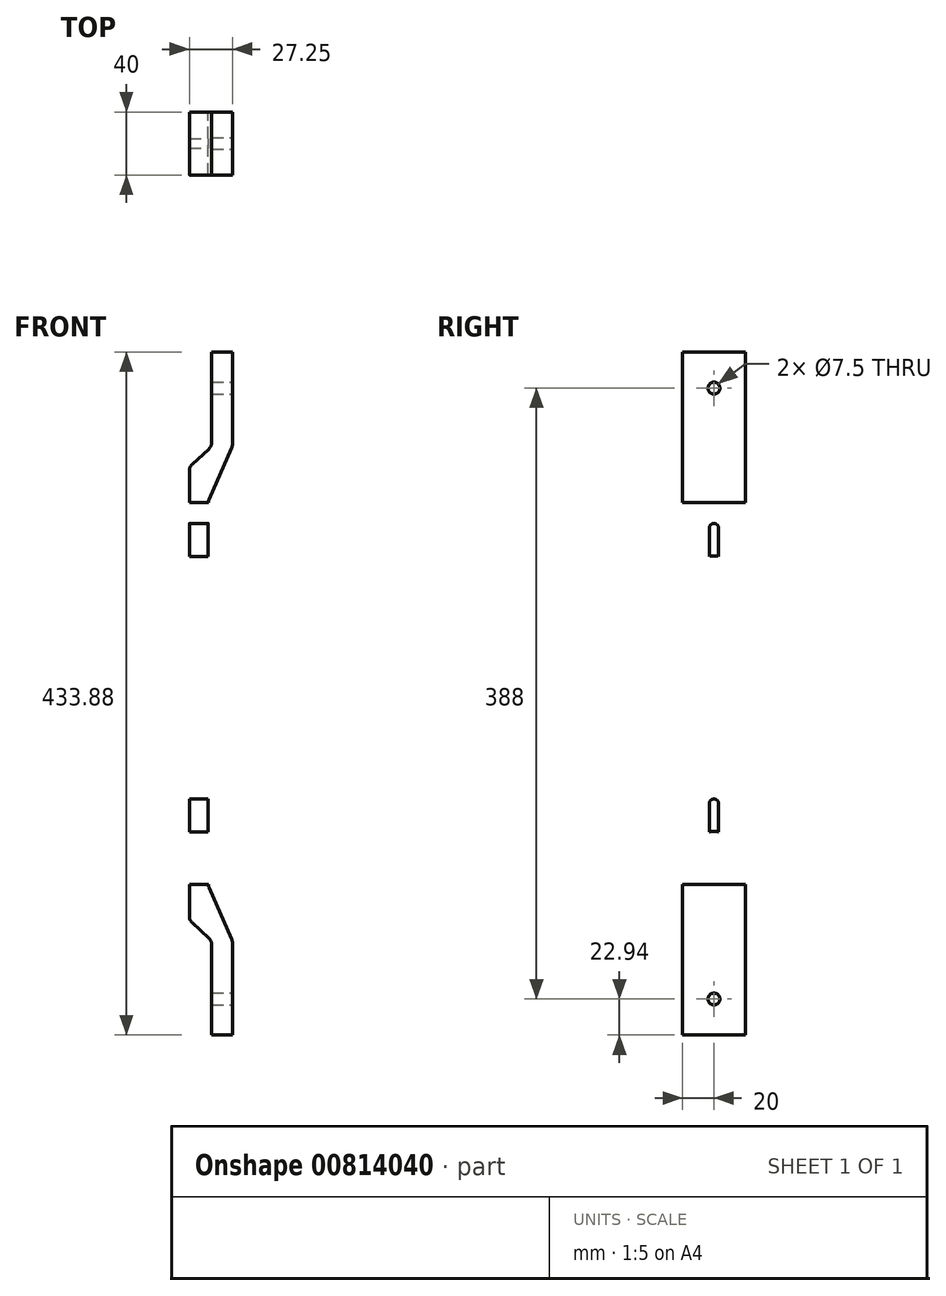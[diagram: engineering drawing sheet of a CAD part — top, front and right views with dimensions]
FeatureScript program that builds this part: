
annotation { "Feature Type Name" : "Feature", "Feature Type Description" : "" }
export const myFeature = defineFeature(function(context is Context, id is Id, definition is map)
    precondition{}
    {
        {
            var Q0;
            Q0=qCreatedBy(makeId("Front.planeOp"),FACE);
            var sketch = newSketch(context, id + "F0", { "sketchPlane" : qUnion([Q0])});
            skLineSegment(sketch, "E0.bottom", {"start": v(-6, 144) * mm, "end": v(6, 144) * mm});
            skLineSegment(sketch, "E0.top", {"start": v(-6, -144) * mm, "end": v(6, -144) * mm});
            skLineSegment(sketch, "E0.left", {"start": v(-6, 144) * mm, "end": v(-6, -144) * mm});
            skLineSegment(sketch, "E0.right", {"start": v(6, 144) * mm, "end": v(6, -144) * mm});
            skPoint(sketch, "E0.middle", {"position": v(0, 0) * mm});
            skLineSegment(sketch, "E1", {"start": v(6, 144) * mm, "end": v(21.25, 156.94) * mm});
            skLineSegment(sketch, "E2", {"start": v(21.25, 156.94) * mm, "end": v(21.25, 216.94) * mm});
            skLineSegment(sketch, "E3", {"start": v(21.25, 216.94) * mm, "end": v(8.03, 216.94) * mm});
            skLineSegment(sketch, "E4", {"start": v(21.25, 156.94) * mm, "end": v(-79.36, 156.94) * mm, "construction": true});
            skLineSegment(sketch, "E5", {"start": v(-6, 136.3) * mm, "end": v(-6, 185.52) * mm, "construction": true});
            skLineSegment(sketch, "E6", {"start": v(8.03, 216.94) * mm, "end": v(8.03, 156.94) * mm});
            skLineSegment(sketch, "E7", {"start": v(8.03, 156.94) * mm, "end": v(-6, 144) * mm});
            skLineSegment(sketch, "E8.MirrorCS", {"start": v(6, -144) * mm, "end": v(21.25, -156.94) * mm});
            skLineSegment(sketch, "E9.MirrorCS", {"start": v(21.25, -216.94) * mm, "end": v(8.03, -216.94) * mm});
            skLineSegment(sketch, "E10.MirrorCS", {"start": v(21.25, -156.94) * mm, "end": v(21.25, -216.94) * mm});
            skLineSegment(sketch, "E11.MirrorCS", {"start": v(8.03, -156.94) * mm, "end": v(-6, -144) * mm});
            skLineSegment(sketch, "E12.MirrorCS", {"start": v(8.03, -216.94) * mm, "end": v(8.03, -156.94) * mm});
            skLineSegment(sketch, "E13.MirrorCS", {"start": v(-6, -136.3) * mm, "end": v(-6, -185.52) * mm, "construction": true});
            skLineSegment(sketch, "E14", {"start": v(21.25, 156.94) * mm, "end": v(6, 122.3) * mm});
            skLineSegment(sketch, "E15.MirrorCS", {"start": v(21.25, -156.94) * mm, "end": v(6, -122.3) * mm});
            skSolve(sketch);
        }
        {
            var Q0;
            Q0 = qSketchRegion(id + "F0", true);
            extrude(context, id + "F1", {"entities" : qUnion([Q0]), "depth" : 40 * mm, "offsetDistance" : 25 * mm});
        }
        {
            var Q0;
            Q0=makeQuery(id+"F1.opExtrude","SWEPT_EDGE",EDGE,{"disambiguationData":[OSD([sQuery(id+"F0.wireOp",EDGE,"E0.right"),sQuery(id+"F0.wireOp",EDGE,"E15.MirrorCS")])]});
            var Q1;
            Q1=makeQuery(id+"F1.opExtrude","SWEPT_EDGE",EDGE,{"disambiguationData":[OSD([sQuery(id+"F0.wireOp",EDGE,"E8.MirrorCS"),sQuery(id+"F0.wireOp",EDGE,"E10.MirrorCS"),sQuery(id+"F0.wireOp",EDGE,"E15.MirrorCS")])]});
            var Q2;
            Q2=makeQuery(id+"F1.opExtrude","SWEPT_EDGE",EDGE,{"disambiguationData":[OSD([sQuery(id+"F0.wireOp",EDGE,"E11.MirrorCS"),sQuery(id+"F0.wireOp",EDGE,"E12.MirrorCS")])]});
            var Q3;
            Q3=makeQuery(id+"F1.opExtrude","SWEPT_EDGE",EDGE,{"disambiguationData":[OSD([sQuery(id+"F0.wireOp",EDGE,"E0.left"),sQuery(id+"F0.wireOp",EDGE,"E0.top"),sQuery(id+"F0.wireOp",EDGE,"E11.MirrorCS")])]});
            var Q4;
            Q4=makeQuery(id+"F1.opExtrude","SWEPT_EDGE",EDGE,{"disambiguationData":[OSD([sQuery(id+"F0.wireOp",EDGE,"E0.bottom"),sQuery(id+"F0.wireOp",EDGE,"E0.left"),sQuery(id+"F0.wireOp",EDGE,"E7")])]});
            var Q5;
            Q5=makeQuery(id+"F1.opExtrude","SWEPT_EDGE",EDGE,{"disambiguationData":[OSD([sQuery(id+"F0.wireOp",EDGE,"E0.right"),sQuery(id+"F0.wireOp",EDGE,"E14")])]});
            var Q6;
            Q6=makeQuery(id+"F1.opExtrude","SWEPT_EDGE",EDGE,{"disambiguationData":[OSD([sQuery(id+"F0.wireOp",EDGE,"E1"),sQuery(id+"F0.wireOp",EDGE,"E2"),sQuery(id+"F0.wireOp",EDGE,"E14")])]});
            fillet(context, id + "F2", {"entities" : qUnion([Q0, Q1, Q2, Q3, Q4, Q5, Q6]), "radius" : 5 * mm, "tangentPropagation" : true, "allowEdgeOverflow" : false});
        }
        {
            var Q0;
            Q0=makeQuery(id+"F1.opExtrude","SWEPT_EDGE",EDGE,{"disambiguationData":[OSD([sQuery(id+"F0.wireOp",EDGE,"E6"),sQuery(id+"F0.wireOp",EDGE,"E7")])]});
            fillet(context, id + "F3", {"entities" : qUnion([Q0]), "radius" : 5 * mm, "tangentPropagation" : true, "allowEdgeOverflow" : false});
        }
        {
            var Q0;
            Q0=makeQuery(id+"F1.opExtrude","SWEPT_FACE",FACE,{"disambiguationData":[OSD([sQuery(id+"F0.wireOp",EDGE,"E2")])]});
            var sketch = newSketch(context, id + "F4", { "sketchPlane" : qUnion([Q0])});
            skPoint(sketch, "E16", {"position": v(-20, 194) * mm});
            skPoint(sketch, "E17.MirrorP", {"position": v(-20, -194) * mm});
            skSolve(sketch);
        }
        {
            var Q0;
            Q0=sQuery(id+"F4.wireOp",VERTEX,"E16");
            var Q1;
            Q1=sQuery(id+"F4.wireOp",VERTEX,"E17.MirrorP");
            var Q2;
            Q2=makeQuery(id+"F1.opExtrude","SWEPT_BODY",BODY,{"disambiguationData":[OSD([sQuery(id+"F0.wireOp",EDGE,"E0.left"),sQuery(id+"F0.wireOp",EDGE,"E0.right"),sQuery(id+"F0.wireOp",EDGE,"E2"),sQuery(id+"F0.wireOp",EDGE,"E3"),sQuery(id+"F0.wireOp",EDGE,"E6"),sQuery(id+"F0.wireOp",EDGE,"E7"),sQuery(id+"F0.wireOp",EDGE,"E9.MirrorCS"),sQuery(id+"F0.wireOp",EDGE,"E10.MirrorCS"),sQuery(id+"F0.wireOp",EDGE,"E11.MirrorCS"),sQuery(id+"F0.wireOp",EDGE,"E12.MirrorCS"),sQuery(id+"F0.wireOp",EDGE,"E14"),sQuery(id+"F0.wireOp",EDGE,"E15.MirrorCS")])]});
            hole(context, id + "F5", {"style" : HoleStyle.SIMPLE, "endStyle" : HoleEndStyle.THROUGH, "holeDiameter" : 7.5 * mm, "majorDiameter" : 5 * mm, "isTappedThrough" : true, "tappedDepth" : 12 * mm, "tapClearance" : 3, "startFromSketch" : true, "locations" : qUnion([Q0, Q1]), "scope" : qUnion([Q2])});
        }
        {
            var Q0;
            Q0=makeQuery(id+"F1.opExtrude","SWEPT_FACE",FACE,{"disambiguationData":[OSD([sQuery(id+"F0.wireOp",EDGE,"E0.right")])]});
            var sketch = newSketch(context, id + "F6", { "sketchPlane" : qUnion([Q0])});
            skPoint(sketch, "E18", {"position": v(-20, 75) * mm});
            skCircle(sketch, "E19", {"center": v(-20, 75) * mm, "radius": 12.5 * mm});
            skLineSegment(sketch, "E20", {"start": v(-20, 75) * mm, "end": v(-20, 105) * mm});
            skArc(sketch, "E21.0.startCap", {"start": v(-17, 75) * mm, "mid": v(-20, 72) * mm, "end": v(-23, 75) * mm});
            skArc(sketch, "E21.0.endCap", {"start": v(-23, 105) * mm, "mid": v(-20, 108) * mm, "end": v(-17, 105) * mm});
            skLineSegment(sketch, "E21.0.left", {"start": v(-23, 75) * mm, "end": v(-23, 105) * mm});
            skLineSegment(sketch, "E21.0.right", {"start": v(-17, 75) * mm, "end": v(-17, 105) * mm});
            skCircle(sketch, "E22", {"center": v(-20, -100) * mm, "radius": 12.5 * mm});
            skLineSegment(sketch, "E23", {"start": v(-20, -100) * mm, "end": v(-20, -70) * mm});
            skArc(sketch, "E24.0.startCap", {"start": v(-17, -100) * mm, "mid": v(-20, -103) * mm, "end": v(-23, -100) * mm});
            skArc(sketch, "E24.0.endCap", {"start": v(-23, -70) * mm, "mid": v(-20, -67) * mm, "end": v(-17, -70) * mm});
            skLineSegment(sketch, "E24.0.left", {"start": v(-23, -100) * mm, "end": v(-23, -70) * mm});
            skLineSegment(sketch, "E24.0.right", {"start": v(-17, -100) * mm, "end": v(-17, -70) * mm});
            skSolve(sketch);
        }
        {
            var Q0;
            {var subQ0=sQuery(id+"F6.wireOp",EDGE,"E24.0.startCap");Q0=makeQuery(id+"F6.imprint","IMPRINT",FACE,{"disambiguationData":[TD([[makeQuery(id+"F6.imprint","IMPRINT",EDGE,{"derivedFrom":subQ0}),-1.0]])]});}
            var Q1;
            {var subQ5=sQuery(id+"F6.wireOp",EDGE,"E24.0.startCap");Q1=makeQuery(id+"F6.imprint","IMPRINT",FACE,{"disambiguationData":[TD([[makeQuery(id+"F6.imprint","IMPRINT",EDGE,{"derivedFrom":subQ5}),1.0]])]});}
            var Q2;
            {var subQ5=sQuery(id+"F6.wireOp",EDGE,"E21.0.startCap");Q2=makeQuery(id+"F6.imprint","IMPRINT",FACE,{"disambiguationData":[TD([[makeQuery(id+"F6.imprint","IMPRINT",EDGE,{"derivedFrom":subQ5}),1.0]])]});}
            var Q3;
            {var subQ0=sQuery(id+"F6.wireOp",EDGE,"E21.0.startCap");Q3=makeQuery(id+"F6.imprint","IMPRINT",FACE,{"disambiguationData":[TD([[makeQuery(id+"F6.imprint","IMPRINT",EDGE,{"derivedFrom":subQ0}),-1.0]])]});}
            var Q4;
            {var subQ0=sQuery(id+"F6.wireOp",EDGE,"E21.0.endCap");Q4=makeQuery(id+"F6.imprint","IMPRINT",FACE,{"disambiguationData":[TD([[makeQuery(id+"F6.imprint","IMPRINT",EDGE,{"derivedFrom":subQ0}),-1.0]])]});}
            var Q5;
            {var subQ0=sQuery(id+"F6.wireOp",EDGE,"E24.0.endCap");Q5=makeQuery(id+"F6.imprint","IMPRINT",FACE,{"disambiguationData":[TD([[makeQuery(id+"F6.imprint","IMPRINT",EDGE,{"derivedFrom":subQ0}),-1.0]])]});}
            extrude(context, id + "F7", {"entities" : qUnion([Q0, Q1, Q2, Q3, Q4, Q5]), "operationType" : NewBodyOperationType.REMOVE, "oppositeDirection" : true, "depth" : 12 * mm, "offsetDistance" : 25 * mm});
        }
    });
